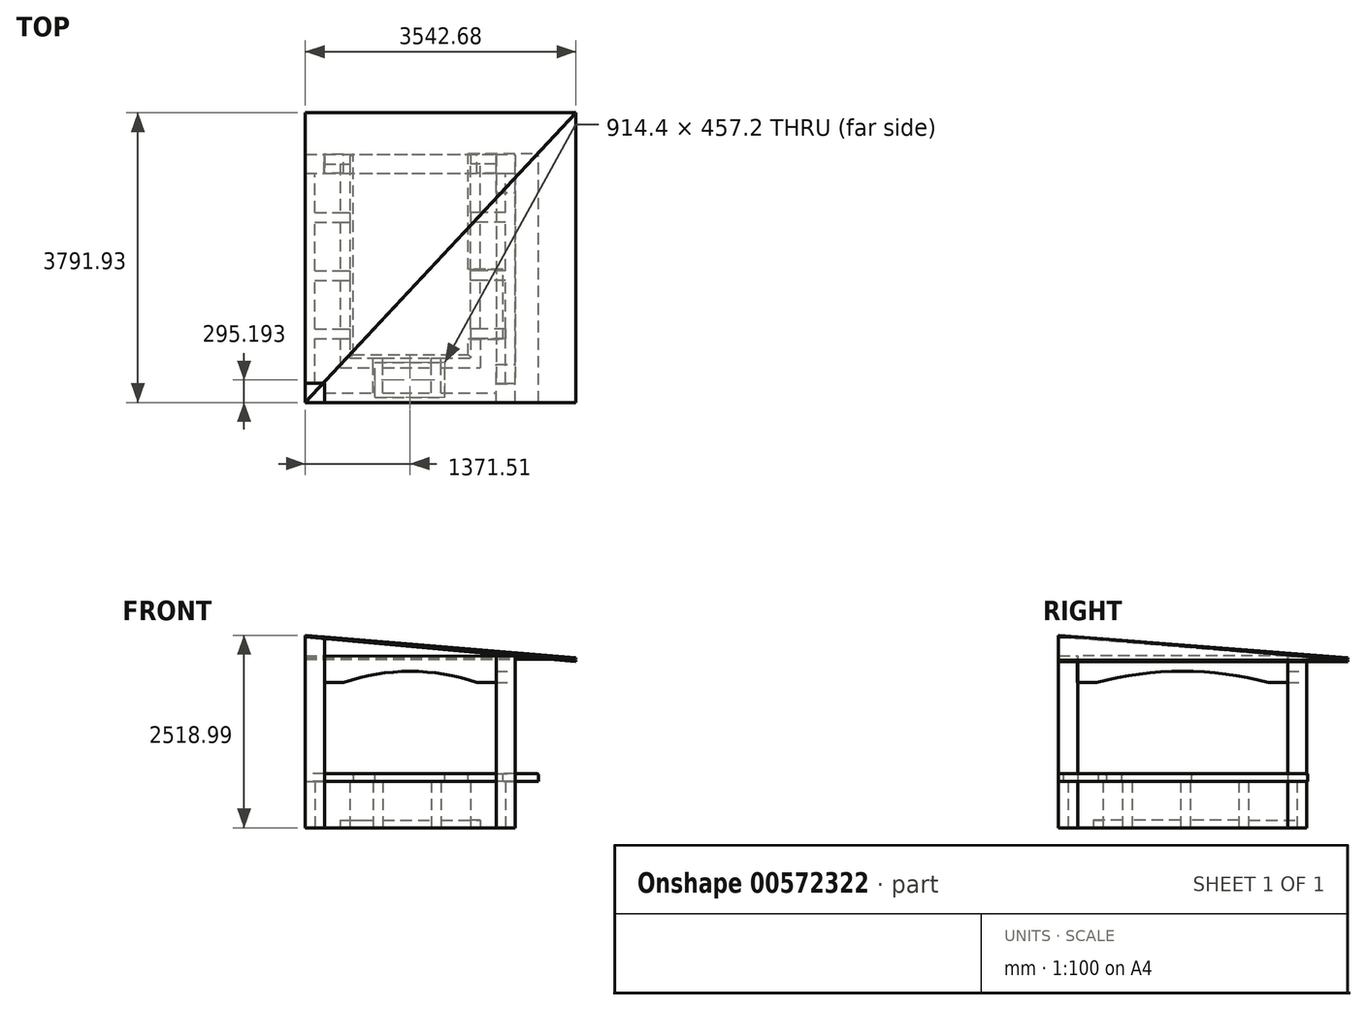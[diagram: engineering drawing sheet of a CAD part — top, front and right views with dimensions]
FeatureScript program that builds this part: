
annotation { "Feature Type Name" : "Feature", "Feature Type Description" : "" }
export const myFeature = defineFeature(function(context is Context, id is Id, definition is map)
    precondition{}
    {
        {
            var Q0;
            Q0=qCreatedBy(makeId("Top.planeOp"),FACE);
            var sketch = newSketch(context, id + "F0", { "sketchPlane" : qUnion([Q0])});
            skLineSegment(sketch, "E0.bottom", {"start": v(0, 0) * mm, "end": v(250, 0) * mm});
            skLineSegment(sketch, "E0.top", {"start": v(0, 250) * mm, "end": v(250, 250) * mm});
            skLineSegment(sketch, "E0.left", {"start": v(0, 0) * mm, "end": v(0, 250) * mm});
            skLineSegment(sketch, "E0.right", {"start": v(250, 0) * mm, "end": v(250, 250) * mm});
            skLineSegment(sketch, "E1.0.1.0", {"start": v(0, 3250) * mm, "end": v(250, 3250) * mm});
            skLineSegment(sketch, "E1.0.1.1", {"start": v(0, 3000) * mm, "end": v(0, 3250) * mm});
            skLineSegment(sketch, "E1.0.1.2", {"start": v(0, 3000) * mm, "end": v(250, 3000) * mm});
            skLineSegment(sketch, "E1.0.1.3", {"start": v(250, 3000) * mm, "end": v(250, 3250) * mm});
            skLineSegment(sketch, "E1.1.0.0", {"start": v(2500, 250) * mm, "end": v(2750, 250) * mm});
            skLineSegment(sketch, "E1.1.0.1", {"start": v(2500, 0) * mm, "end": v(2500, 250) * mm});
            skLineSegment(sketch, "E1.1.0.2", {"start": v(2500, 0) * mm, "end": v(2750, 0) * mm});
            skLineSegment(sketch, "E1.1.0.3", {"start": v(2750, 0) * mm, "end": v(2750, 250) * mm});
            skLineSegment(sketch, "E1.1.1.0", {"start": v(2500, 3250) * mm, "end": v(2750, 3250) * mm});
            skLineSegment(sketch, "E1.1.1.1", {"start": v(2500, 3000) * mm, "end": v(2500, 3250) * mm});
            skLineSegment(sketch, "E1.1.1.2", {"start": v(2500, 3000) * mm, "end": v(2750, 3000) * mm});
            skLineSegment(sketch, "E1.1.1.3", {"start": v(2750, 3000) * mm, "end": v(2750, 3250) * mm});
            skLineSegment(sketch, "E1.direction2", {"start": v(0, 250) * mm, "end": v(0, 3250) * mm, "construction": true});
            skLineSegment(sketch, "E2.bottom", {"start": v(0, 250) * mm, "end": v(127, 250) * mm});
            skLineSegment(sketch, "E2.top", {"start": v(0, 3250) * mm, "end": v(127, 3250) * mm});
            skLineSegment(sketch, "E2.left", {"start": v(0, 250) * mm, "end": v(0, 3250) * mm});
            skLineSegment(sketch, "E2.right", {"start": v(127, 250) * mm, "end": v(127, 3000) * mm});
            skLineSegment(sketch, "E3.bottom", {"start": v(250, 0) * mm, "end": v(2750, 0) * mm});
            skLineSegment(sketch, "E3.top", {"start": v(250, 127) * mm, "end": v(2500, 127) * mm});
            skLineSegment(sketch, "E3.left", {"start": v(250, 0) * mm, "end": v(250, 127) * mm});
            skLineSegment(sketch, "E3.right", {"start": v(2750, 0) * mm, "end": v(2750, 127) * mm});
            skLineSegment(sketch, "E4.top", {"start": v(2750, 3250) * mm, "end": v(2623, 3250) * mm});
            skLineSegment(sketch, "E4.left", {"start": v(2750, 127) * mm, "end": v(2750, 3250) * mm});
            skLineSegment(sketch, "E4.right", {"start": v(2623, 250) * mm, "end": v(2623, 3000) * mm});
            skLineSegment(sketch, "E5.bottom", {"start": v(2623, 3250) * mm, "end": v(2165.8, 3250) * mm});
            skLineSegment(sketch, "E5.top", {"start": v(2500, 3123) * mm, "end": v(2165.8, 3123) * mm});
            skLineSegment(sketch, "E5.right", {"start": v(2165.8, 3250) * mm, "end": v(2165.8, 3123) * mm});
            skLineSegment(sketch, "E6.bottom", {"start": v(127, 3250) * mm, "end": v(584.2, 3250) * mm});
            skLineSegment(sketch, "E6.top", {"start": v(250, 3123) * mm, "end": v(584.2, 3123) * mm});
            skLineSegment(sketch, "E6.right", {"start": v(584.2, 3250) * mm, "end": v(584.2, 3123) * mm});
            skLineSegment(sketch, "E7.0.1.0", {"start": v(127, 2488) * mm, "end": v(584.2, 2488) * mm});
            skLineSegment(sketch, "E7.0.1.1", {"start": v(127, 2361) * mm, "end": v(584.2, 2361) * mm});
            skLineSegment(sketch, "E7.0.1.2", {"start": v(584.2, 2488) * mm, "end": v(584.2, 2361) * mm});
            skLineSegment(sketch, "E7.0.1.3", {"start": v(127, 2488) * mm, "end": v(127, 2361) * mm});
            skLineSegment(sketch, "E7.0.2.0", {"start": v(127, 1726) * mm, "end": v(584.2, 1726) * mm});
            skLineSegment(sketch, "E7.0.2.1", {"start": v(127, 1599) * mm, "end": v(584.2, 1599) * mm});
            skLineSegment(sketch, "E7.0.2.2", {"start": v(584.2, 1726) * mm, "end": v(584.2, 1599) * mm});
            skLineSegment(sketch, "E7.0.2.3", {"start": v(127, 1726) * mm, "end": v(127, 1599) * mm});
            skLineSegment(sketch, "E7.direction2", {"start": v(127, 3000) * mm, "end": v(127, 2488) * mm, "construction": true});
            skLineSegment(sketch, "E8.0.1.0", {"start": v(2623, 2361) * mm, "end": v(2165.8, 2361) * mm});
            skLineSegment(sketch, "E8.0.1.1", {"start": v(2623, 2488) * mm, "end": v(2165.8, 2488) * mm});
            skLineSegment(sketch, "E8.0.1.2", {"start": v(2623, 2488) * mm, "end": v(2623, 2361) * mm});
            skLineSegment(sketch, "E8.0.1.3", {"start": v(2165.8, 2488) * mm, "end": v(2165.8, 2361) * mm});
            skLineSegment(sketch, "E8.0.2.0", {"start": v(2623.2, 836.8) * mm, "end": v(2166, 836.8) * mm});
            skLineSegment(sketch, "E8.0.2.1", {"start": v(2623.2, 964) * mm, "end": v(2166, 964) * mm});
            skLineSegment(sketch, "E8.0.2.2", {"start": v(2623.2, 964) * mm, "end": v(2623.2, 836.8) * mm});
            skLineSegment(sketch, "E8.0.2.3", {"start": v(2166, 964) * mm, "end": v(2166, 836.8) * mm});
            skLineSegment(sketch, "E8.direction2", {"start": v(2165.8, 3123) * mm, "end": v(2165.8, 2361) * mm, "construction": true});
            skLineSegment(sketch, "E9.bottom", {"start": v(889, 127) * mm, "end": v(1016, 127) * mm});
            skLineSegment(sketch, "E9.top", {"start": v(889, 584.2) * mm, "end": v(1016, 584.2) * mm});
            skLineSegment(sketch, "E9.left", {"start": v(889, 127) * mm, "end": v(889, 584.2) * mm});
            skLineSegment(sketch, "E9.right", {"start": v(1016, 127) * mm, "end": v(1016, 584.2) * mm});
            skLineSegment(sketch, "E10.1.0.0", {"start": v(1651, 127) * mm, "end": v(1651, 584.2) * mm});
            skLineSegment(sketch, "E10.1.0.1", {"start": v(1778, 127) * mm, "end": v(1778, 584.2) * mm});
            skLineSegment(sketch, "E10.1.0.2", {"start": v(1651, 127) * mm, "end": v(1778, 127) * mm});
            skLineSegment(sketch, "E10.1.0.3", {"start": v(1651, 584.2) * mm, "end": v(1778, 584.2) * mm});
            skLineSegment(sketch, "E11.bottom", {"start": v(584.2, 3123) * mm, "end": v(457.2, 3123) * mm});
            skLineSegment(sketch, "E11.top", {"start": v(584.2, 2488) * mm, "end": v(457.2, 2488) * mm});
            skLineSegment(sketch, "E11.left", {"start": v(584.2, 3123) * mm, "end": v(584.2, 2488) * mm});
            skLineSegment(sketch, "E11.right", {"start": v(457.2, 3123) * mm, "end": v(457.2, 2488) * mm});
            skLineSegment(sketch, "E12.bottom", {"start": v(584.2, 2361) * mm, "end": v(457.2, 2361) * mm});
            skLineSegment(sketch, "E12.top", {"start": v(584.2, 1726) * mm, "end": v(457.2, 1726) * mm});
            skLineSegment(sketch, "E12.left", {"start": v(584.2, 2361) * mm, "end": v(584.2, 1726) * mm});
            skLineSegment(sketch, "E12.right", {"start": v(457.2, 2361) * mm, "end": v(457.2, 1726) * mm});
            skLineSegment(sketch, "E13.bottom", {"start": v(584.2, 1599) * mm, "end": v(457.2, 1599) * mm});
            skLineSegment(sketch, "E13.top", {"start": v(584.2, 584.2) * mm, "end": v(457.2, 584.2) * mm});
            skLineSegment(sketch, "E13.left", {"start": v(584.2, 1599) * mm, "end": v(584.2, 584.2) * mm});
            skLineSegment(sketch, "E13.right", {"start": v(457.2, 1599) * mm, "end": v(457.2, 964) * mm});
            skLineSegment(sketch, "E14.bottom", {"start": v(457.2, 584.2) * mm, "end": v(889, 584.2) * mm});
            skLineSegment(sketch, "E14.top", {"start": v(457.2, 457.2) * mm, "end": v(889, 457.2) * mm});
            skLineSegment(sketch, "E14.left", {"start": v(457.2, 584.2) * mm, "end": v(457.2, 457.2) * mm});
            skLineSegment(sketch, "E14.right", {"start": v(889, 584.2) * mm, "end": v(889, 457.2) * mm});
            skLineSegment(sketch, "E15.bottom", {"start": v(1016, 584.2) * mm, "end": v(1651, 584.2) * mm});
            skLineSegment(sketch, "E15.top", {"start": v(1016, 457.2) * mm, "end": v(1651, 457.2) * mm});
            skLineSegment(sketch, "E15.left", {"start": v(1016, 584.2) * mm, "end": v(1016, 457.2) * mm});
            skLineSegment(sketch, "E15.right", {"start": v(1651, 584.2) * mm, "end": v(1651, 457.2) * mm});
            skLineSegment(sketch, "E16.bottom", {"start": v(1778, 584.2) * mm, "end": v(2293, 584.2) * mm});
            skLineSegment(sketch, "E16.left", {"start": v(1778, 584.2) * mm, "end": v(1778, 457.2) * mm});
            skLineSegment(sketch, "E17.bottom", {"start": v(2166, 836.8) * mm, "end": v(2293, 836.8) * mm});
            skLineSegment(sketch, "E17.top", {"start": v(1778, 457.2) * mm, "end": v(2293, 457.2) * mm});
            skLineSegment(sketch, "E17.right", {"start": v(2293, 836.8) * mm, "end": v(2293, 457.2) * mm});
            skLineSegment(sketch, "E18.bottom", {"start": v(2166, 964) * mm, "end": v(2293, 964) * mm});
            skLineSegment(sketch, "E18.top", {"start": v(2166, 2361) * mm, "end": v(2293, 2361) * mm});
            skLineSegment(sketch, "E18.left", {"start": v(2166, 964) * mm, "end": v(2166, 2361) * mm});
            skLineSegment(sketch, "E18.right", {"start": v(2293, 964) * mm, "end": v(2293, 1599) * mm});
            skLineSegment(sketch, "E19.bottom", {"start": v(2165.8, 2488) * mm, "end": v(2293, 2488) * mm});
            skLineSegment(sketch, "E19.top", {"start": v(2165.8, 3123) * mm, "end": v(2293, 3123) * mm});
            skLineSegment(sketch, "E19.left", {"start": v(2165.8, 2488) * mm, "end": v(2165.8, 3123) * mm});
            skLineSegment(sketch, "E19.right", {"start": v(2293, 2488) * mm, "end": v(2293, 3123) * mm});
            skLineSegment(sketch, "E20.0.0.3", {"start": v(127, 964) * mm, "end": v(584.2, 964) * mm});
            skLineSegment(sketch, "E20.3.0.3", {"start": v(127, 837) * mm, "end": v(584.2, 837) * mm});
            skLineSegment(sketch, "E20.6.0.3", {"start": v(584.2, 964) * mm, "end": v(584.2, 837) * mm});
            skLineSegment(sketch, "E20.9.0.3", {"start": v(127, 964) * mm, "end": v(127, 837) * mm});
            skLineSegment(sketch, "E21.bottom", {"start": v(2623, 1726) * mm, "end": v(2166, 1726) * mm});
            skLineSegment(sketch, "E21.top", {"start": v(2623, 1599) * mm, "end": v(2166, 1599) * mm});
            skLineSegment(sketch, "E21.left", {"start": v(2623, 1726) * mm, "end": v(2623, 1599) * mm});
            skLineSegment(sketch, "E21.right", {"start": v(2166, 1726) * mm, "end": v(2166, 1599) * mm});
            skLineSegment(sketch, "E22.trimOffspring", {"start": v(2293, 1726) * mm, "end": v(2293, 2361) * mm});
            skLineSegment(sketch, "E23.trimOffspring", {"start": v(457.2, 837) * mm, "end": v(457.2, 584.2) * mm});
            skLineSegment(sketch, "E24", {"start": v(2166, 836.8) * mm, "end": v(2166, 584.2) * mm});
            skSolve(sketch);
        }
        {
            var Q0;
            {var subQ4=sQuery(id+"F0.wireOp",EDGE,"E0.top");Q0=makeQuery(id+"F0.imprint","IMPRINT",FACE,{"disambiguationData":[TD([[makeQuery(id+"F0.imprint","IMPRINT",EDGE,{"derivedFrom":subQ4}),-1.0]])]});}
            extrude(context, id + "F1", {"entities" : qUnion([Q0]), "depth" : 2500 * mm, "offsetDistance" : 25.4 * mm});
        }
        {
            var Q0;
            {var subQ0=sQuery(id+"F0.wireOp",EDGE,"E1.0.1.0");Q0=makeQuery(id+"F0.imprint","IMPRINT",FACE,{"disambiguationData":[TD([[makeQuery(id+"F0.imprint","IMPRINT",EDGE,{"derivedFrom":subQ0}),-1.0]])]});}
            extrude(context, id + "F2", {"entities" : qUnion([Q0]), "depth" : 2250 * mm, "offsetDistance" : 25 * mm});
        }
        {
            var Q0;
            Q0=makeQuery(id+"F0.imprint","IMPRINT",FACE,{"disambiguationData":[TD([[makeQuery(id+"F0.imprint","IMPRINT",EDGE,{"derivedFrom":sQuery(id+"F0.wireOp",EDGE,"E1.1.0.0")}),-1.0]])]});
            extrude(context, id + "F3", {"entities" : qUnion([Q0]), "depth" : 2250 * mm, "offsetDistance" : 25 * mm});
        }
        {
            var Q0;
            Q0=makeQuery(id+"F0.imprint","IMPRINT",FACE,{"disambiguationData":[TD([[makeQuery(id+"F0.imprint","IMPRINT",EDGE,{"derivedFrom":sQuery(id+"F0.wireOp",EDGE,"E1.1.1.0")}),-1.0]])]});
            extrude(context, id + "F4", {"entities" : qUnion([Q0]), "depth" : 2250 * mm, "offsetDistance" : 25 * mm});
        }
        {
            var Q0;
            {var subQ5=sQuery(id+"F0.wireOp",EDGE,"E6.bottom");Q0=makeQuery(id+"F0.imprint","IMPRINT",FACE,{"disambiguationData":[TD([[makeQuery(id+"F0.imprint","IMPRINT",EDGE,{"derivedFrom":subQ5}),-1.0]])]});}
            var Q1;
            {var subQ0=sQuery(id+"F0.wireOp",EDGE,"E2.left");Q1=makeQuery(id+"F0.imprint","IMPRINT",FACE,{"disambiguationData":[TD([[makeQuery(id+"F0.imprint","IMPRINT",EDGE,{"derivedFrom":subQ0}),-1.0]])]});}
            var Q2;
            {var subQ0=sQuery(id+"F0.wireOp",EDGE,"E7.0.1.2");Q2=makeQuery(id+"F0.imprint","IMPRINT",FACE,{"disambiguationData":[TD([[makeQuery(id+"F0.imprint","IMPRINT",EDGE,{"derivedFrom":subQ0}),-1.0]])]});}
            var Q3;
            {var subQ4=sQuery(id+"F0.wireOp",EDGE,"E7.0.2.2");Q3=makeQuery(id+"F0.imprint","IMPRINT",FACE,{"disambiguationData":[TD([[makeQuery(id+"F0.imprint","IMPRINT",EDGE,{"derivedFrom":subQ4}),-1.0]])]});}
            var Q4;
            {var subQ0=sQuery(id+"F0.wireOp",EDGE,"E20.0.0.3");var subQ4=sQuery(id+"F0.wireOp",EDGE,"E2.right");var subQ5=makeQuery(id+"F0.imprint","INTERSECT",VERTEX,{"derivedFrom":[subQ4,subQ0]});Q4=makeQuery(id+"F0.imprint","IMPRINT",FACE,{"disambiguationData":[TD([[makeQuery(id+"F0.imprint","IMPRINT",EDGE,{"disambiguationData":[TD([[subQ5,1.0]])],"derivedFrom":subQ4}),-1.0]])]});}
            var Q5;
            {var subQ1=sQuery(id+"F0.wireOp",EDGE,"E9.top");Q5=makeQuery(id+"F0.imprint","IMPRINT",FACE,{"disambiguationData":[TD([[makeQuery(id+"F0.imprint","IMPRINT",EDGE,{"derivedFrom":subQ1}),-1.0]])]});}
            var Q6;
            {var subQ4=sQuery(id+"F0.wireOp",EDGE,"E10.1.0.3");Q6=makeQuery(id+"F0.imprint","IMPRINT",FACE,{"disambiguationData":[TD([[makeQuery(id+"F0.imprint","IMPRINT",EDGE,{"derivedFrom":subQ4}),-1.0]])]});}
            var Q7;
            {var subQ0=sQuery(id+"F0.wireOp",EDGE,"E3.bottom");Q7=makeQuery(id+"F0.imprint","IMPRINT",FACE,{"disambiguationData":[TD([[makeQuery(id+"F0.imprint","IMPRINT",EDGE,{"derivedFrom":subQ0}),1.0]])]});}
            var Q8;
            {var subQ13=sQuery(id+"F0.wireOp",EDGE,"E4.left");Q8=makeQuery(id+"F0.imprint","IMPRINT",FACE,{"disambiguationData":[TD([[makeQuery(id+"F0.imprint","IMPRINT",EDGE,{"derivedFrom":subQ13}),1.0]])]});}
            var Q9;
            {var subQ0=sQuery(id+"F0.wireOp",EDGE,"E8.0.2.3");Q9=makeQuery(id+"F0.imprint","IMPRINT",FACE,{"disambiguationData":[TD([[makeQuery(id+"F0.imprint","IMPRINT",EDGE,{"derivedFrom":subQ0}),1.0]])]});}
            var Q10;
            {var subQ0=sQuery(id+"F0.wireOp",EDGE,"E21.bottom");var subQ4=sQuery(id+"F0.wireOp",EDGE,"E4.right");var subQ5=makeQuery(id+"F0.imprint","INTERSECT",VERTEX,{"derivedFrom":[subQ4,subQ0]});Q10=makeQuery(id+"F0.imprint","IMPRINT",FACE,{"disambiguationData":[TD([[makeQuery(id+"F0.imprint","IMPRINT",EDGE,{"disambiguationData":[TD([[subQ5,1.0]])],"derivedFrom":subQ4}),1.0]])]});}
            var Q11;
            {var subQ0=sQuery(id+"F0.wireOp",EDGE,"E8.0.1.3");Q11=makeQuery(id+"F0.imprint","IMPRINT",FACE,{"disambiguationData":[TD([[makeQuery(id+"F0.imprint","IMPRINT",EDGE,{"derivedFrom":subQ0}),1.0]])]});}
            var Q12;
            {var subQ5=sQuery(id+"F0.wireOp",EDGE,"E5.bottom");Q12=makeQuery(id+"F0.imprint","IMPRINT",FACE,{"disambiguationData":[TD([[makeQuery(id+"F0.imprint","IMPRINT",EDGE,{"derivedFrom":subQ5}),1.0]])]});}
            extrude(context, id + "F5", {"entities" : qUnion([Q0, Q1, Q2, Q3, Q4, Q5, Q6, Q7, Q8, Q9, Q10, Q11, Q12]), "depth" : 609.6 * mm, "offsetDistance" : 25 * mm});
        }
        {
            var Q0;
            {var subQ0=sQuery(id+"F0.wireOp",EDGE,"E11.left");Q0=makeQuery(id+"F0.imprint","IMPRINT",FACE,{"disambiguationData":[TD([[makeQuery(id+"F0.imprint","IMPRINT",EDGE,{"derivedFrom":subQ0}),-1.0]])]});}
            var Q1;
            {var subQ0=sQuery(id+"F0.wireOp",EDGE,"E12.left");Q1=makeQuery(id+"F0.imprint","IMPRINT",FACE,{"disambiguationData":[TD([[makeQuery(id+"F0.imprint","IMPRINT",EDGE,{"derivedFrom":subQ0}),-1.0]])]});}
            var Q2;
            {var subQ3=sQuery(id+"F0.wireOp",EDGE,"E13.right");Q2=makeQuery(id+"F0.imprint","IMPRINT",FACE,{"disambiguationData":[TD([[makeQuery(id+"F0.imprint","IMPRINT",EDGE,{"derivedFrom":subQ3}),1.0]])]});}
            var Q3;
            {var subQ0=sQuery(id+"F0.wireOp",EDGE,"E13.top");Q3=makeQuery(id+"F0.imprint","IMPRINT",FACE,{"disambiguationData":[TD([[makeQuery(id+"F0.imprint","IMPRINT",EDGE,{"derivedFrom":subQ0}),-1.0]])]});}
            var Q4;
            Q4=makeQuery(id+"F0.imprint","IMPRINT",FACE,{"disambiguationData":[TD([[makeQuery(id+"F0.imprint","IMPRINT",EDGE,{"derivedFrom":sQuery(id+"F0.wireOp",EDGE,"E13.top")}),1.0]])]});
            var Q5;
            {var subQ0=sQuery(id+"F0.wireOp",EDGE,"E15.bottom");Q5=makeQuery(id+"F0.imprint","IMPRINT",FACE,{"disambiguationData":[TD([[makeQuery(id+"F0.imprint","IMPRINT",EDGE,{"derivedFrom":subQ0}),-1.0]])]});}
            var Q6;
            {var subQ0=sQuery(id+"F0.wireOp",EDGE,"E17.top");Q6=makeQuery(id+"F0.imprint","IMPRINT",FACE,{"disambiguationData":[TD([[makeQuery(id+"F0.imprint","IMPRINT",EDGE,{"derivedFrom":subQ0}),1.0]])]});}
            var Q7;
            {var subQ0=sQuery(id+"F0.wireOp",EDGE,"E24");Q7=makeQuery(id+"F0.imprint","IMPRINT",FACE,{"disambiguationData":[TD([[makeQuery(id+"F0.imprint","IMPRINT",EDGE,{"derivedFrom":subQ0}),1.0]])]});}
            var Q8;
            {var subQ3=sQuery(id+"F0.wireOp",EDGE,"E18.right");Q8=makeQuery(id+"F0.imprint","IMPRINT",FACE,{"disambiguationData":[TD([[makeQuery(id+"F0.imprint","IMPRINT",EDGE,{"derivedFrom":subQ3}),1.0]])]});}
            var Q9;
            {var subQ0=sQuery(id+"F0.wireOp",EDGE,"E22.trimOffspring");Q9=makeQuery(id+"F0.imprint","IMPRINT",FACE,{"disambiguationData":[TD([[makeQuery(id+"F0.imprint","IMPRINT",EDGE,{"derivedFrom":subQ0}),1.0]])]});}
            var Q10;
            {var subQ0=sQuery(id+"F0.wireOp",EDGE,"E19.left");Q10=makeQuery(id+"F0.imprint","IMPRINT",FACE,{"disambiguationData":[TD([[makeQuery(id+"F0.imprint","IMPRINT",EDGE,{"derivedFrom":subQ0}),-1.0]])]});}
            extrude(context, id + "F6", {"entities" : qUnion([Q0, Q1, Q2, Q3, Q4, Q5, Q6, Q7, Q8, Q9, Q10]), "depth" : 101.6 * mm, "offsetDistance" : 25 * mm});
        }
        {
            var Q0;
            Q0=makeQuery(id+"F5.opExtrude","CAP_FACE",FACE,{"disambiguationData":[OSD([sQuery(id+"F0.wireOp",EDGE,"E0.top"),sQuery(id+"F0.wireOp",EDGE,"E1.0.1.2"),sQuery(id+"F0.wireOp",EDGE,"E2.left"),sQuery(id+"F0.wireOp",EDGE,"E2.right"),sQuery(id+"F0.wireOp",EDGE,"E7.0.1.0"),sQuery(id+"F0.wireOp",EDGE,"E7.0.1.1"),sQuery(id+"F0.wireOp",EDGE,"E7.0.1.2"),sQuery(id+"F0.wireOp",EDGE,"E7.0.2.0"),sQuery(id+"F0.wireOp",EDGE,"E7.0.2.1"),sQuery(id+"F0.wireOp",EDGE,"E7.0.2.2"),sQuery(id+"F0.wireOp",EDGE,"E13.left"),sQuery(id+"F0.wireOp",EDGE,"E20.0.0.3"),sQuery(id+"F0.wireOp",EDGE,"E20.3.0.3")])],"isStart":false});
            var sketch = newSketch(context, id + "F7", { "sketchPlane" : qUnion([Q0])});
            skLineSegment(sketch, "E25.bottom", {"start": v(0, 0) * mm, "end": v(625, 0) * mm});
            skLineSegment(sketch, "E25.top", {"start": v(0, 3250) * mm, "end": v(625, 3250) * mm});
            skLineSegment(sketch, "E25.left", {"start": v(0, 0) * mm, "end": v(0, 3250) * mm});
            skLineSegment(sketch, "E25.right", {"start": v(625, 0) * mm, "end": v(625, 3250) * mm});
            skLineSegment(sketch, "E26.bottom", {"start": v(625, 0) * mm, "end": v(2133.48, 0) * mm});
            skLineSegment(sketch, "E26.top", {"start": v(625, 625.4) * mm, "end": v(2133.48, 625.4) * mm});
            skLineSegment(sketch, "E26.left", {"start": v(625, 0) * mm, "end": v(625, 625.4) * mm});
            skLineSegment(sketch, "E26.right", {"start": v(2133.48, 0) * mm, "end": v(2133.48, 625.4) * mm});
            skLineSegment(sketch, "E27.bottom", {"start": v(2133.48, 0) * mm, "end": v(3054.8, 0) * mm});
            skLineSegment(sketch, "E27.top", {"start": v(2133.48, 3263.7) * mm, "end": v(3054.8, 3263.7) * mm});
            skLineSegment(sketch, "E27.left", {"start": v(2133.48, 0) * mm, "end": v(2133.48, 3263.7) * mm});
            skLineSegment(sketch, "E27.right", {"start": v(3054.8, 0) * mm, "end": v(3054.8, 3263.7) * mm});
            skSolve(sketch);
        }
        {
            var Q0;
            Q0 = qSketchRegion(id + "F7", true);
            extrude(context, id + "F8", {"entities" : qUnion([Q0]), "depth" : 101.6 * mm, "offsetDistance" : 25 * mm});
        }
        {
            var Q0;
            Q0=makeQuery(id+"F8.opExtrude","CAP_EDGE",EDGE,{"disambiguationData":[OSD([sQuery(id+"F7.wireOp",EDGE,"E27.right")])],"isStart":false});
            var Q1;
            Q1=makeQuery(id+"F8.opExtrude","CAP_EDGE",EDGE,{"disambiguationData":[OSD([sQuery(id+"F7.wireOp",EDGE,"E27.top")])],"isStart":false});
            var Q2;
            Q2=makeQuery(id+"F8.opExtrude","CAP_EDGE",EDGE,{"disambiguationData":[OSD([sQuery(id+"F7.wireOp",EDGE,"E25.right")])],"isStart":false});
            var Q3;
            Q3=makeQuery(id+"F8.opExtrude","CAP_EDGE",EDGE,{"disambiguationData":[OSD([sQuery(id+"F7.wireOp",EDGE,"E25.top")])],"isStart":false});
            var Q4;
            Q4=makeQuery(id+"F8.opExtrude","CAP_EDGE",EDGE,{"disambiguationData":[OSD([sQuery(id+"F7.wireOp",EDGE,"E26.top")])],"isStart":false});
            var Q5;
            Q5=makeQuery(id+"F8.opExtrude","CAP_EDGE",EDGE,{"disambiguationData":[OSD([sQuery(id+"F7.wireOp",EDGE,"E27.left")])],"isStart":false});
            fillet(context, id + "F9", {"entities" : qUnion([Q0, Q1, Q2, Q3, Q4, Q5]), "tangentPropagation" : true, "radius" : 25.4 * mm, "defaultsChanged" : true, "vertexSettings" : [], "allowEdgeOverflow" : false});
        }
        {
            var Q0;
            Q0=makeQuery(id+"F2.opExtrude","CAP_VERTEX",VERTEX,{"disambiguationData":[OSD([sQuery(id+"F0.wireOp",EDGE,"E1.0.1.0"),sQuery(id+"F0.wireOp",EDGE,"E1.0.1.1")])],"isStart":false});
            var Q1;
            Q1=makeQuery(id+"F4.opExtrude","CAP_VERTEX",VERTEX,{"disambiguationData":[OSD([sQuery(id+"F0.wireOp",EDGE,"E1.1.1.0"),sQuery(id+"F0.wireOp",EDGE,"E1.1.1.3")])],"isStart":false});
            var Q2;
            Q2=makeQuery(id+"F1.opExtrude","CAP_VERTEX",VERTEX,{"disambiguationData":[OSD([sQuery(id+"F0.wireOp",EDGE,"E0.bottom"),sQuery(id+"F0.wireOp",EDGE,"E0.left")])],"isStart":false});
            cPlane(context, id + "F10", {"entities" : qUnion([Q0, Q1, Q2]), "cplaneType" : CPlaneType.THREE_POINT, "offset" : 25 * mm, "width" : 150 * mm, "height" : 150 * mm});
        }
        {
            var Q0;
            Q0=makeQuery(id+"F4.opExtrude","CAP_VERTEX",VERTEX,{"disambiguationData":[OSD([sQuery(id+"F0.wireOp",EDGE,"E1.1.1.0"),sQuery(id+"F0.wireOp",EDGE,"E1.1.1.3")])],"isStart":false});
            var Q1;
            Q1=makeQuery(id+"F3.opExtrude","CAP_VERTEX",VERTEX,{"disambiguationData":[OSD([sQuery(id+"F0.wireOp",EDGE,"E1.1.0.2"),sQuery(id+"F0.wireOp",EDGE,"E1.1.0.3")])],"isStart":false});
            var Q2;
            Q2=makeQuery(id+"F1.opExtrude","CAP_VERTEX",VERTEX,{"disambiguationData":[OSD([sQuery(id+"F0.wireOp",EDGE,"E0.bottom"),sQuery(id+"F0.wireOp",EDGE,"E0.left")])],"isStart":false});
            cPlane(context, id + "F11", {"entities" : qUnion([Q0, Q1, Q2]), "cplaneType" : CPlaneType.THREE_POINT, "offset" : 25 * mm, "width" : 150 * mm, "height" : 150 * mm});
        }
        {
            var Q0;
            Q0=makeQuery(id+"F4.opExtrude","SWEPT_FACE",FACE,{"disambiguationData":[OSD([sQuery(id+"F0.wireOp",EDGE,"E1.1.1.3")])]});
            var sketch = newSketch(context, id + "F12", { "sketchPlane" : qUnion([Q0])});
            skLineSegment(sketch, "E28", {"start": v(247.26, 1900) * mm, "end": v(497.26, 1900) * mm});
            skArc(sketch, "E29", {"start": v(2750, 1900) * mm, "mid": v(1623.63, 2050) * mm, "end": v(497.26, 1900) * mm});
            skLineSegment(sketch, "E30", {"start": v(2750, 1900) * mm, "end": v(3000, 1900) * mm});
            skLineSegment(sketch, "E31", {"start": v(3000, 1900) * mm, "end": v(3000, 2250) * mm});
            skLineSegment(sketch, "E32", {"start": v(3000, 2250) * mm, "end": v(247.26, 2250) * mm});
            skLineSegment(sketch, "E33", {"start": v(247.26, 2250) * mm, "end": v(247.26, 1900) * mm});
            skSolve(sketch);
        }
        {
            var Q0;
            Q0 = qSketchRegion(id + "F12", true);
            extrude(context, id + "F13", {"entities" : qUnion([Q0]), "oppositeDirection" : true, "depth" : 250 * mm, "offsetDistance" : 25 * mm});
        }
        {
            var Q0;
            Q0=makeQuery(id+"F4.opExtrude","SWEPT_FACE",FACE,{"disambiguationData":[OSD([sQuery(id+"F0.wireOp",EDGE,"E1.1.1.0")])]});
            var sketch = newSketch(context, id + "F14", { "sketchPlane" : qUnion([Q0])});
            skLineSegment(sketch, "E34", {"start": v(-2500, 2250) * mm, "end": v(-2500, 1900) * mm});
            skLineSegment(sketch, "E35", {"start": v(-2500, 1900) * mm, "end": v(-2250, 1900) * mm});
            skArc(sketch, "E36", {"start": v(-498.96, 1900) * mm, "mid": v(-1374.48, 2047.9) * mm, "end": v(-2250, 1900) * mm});
            skLineSegment(sketch, "E37", {"start": v(-498.96, 1900) * mm, "end": v(-248.96, 1900) * mm});
            skLineSegment(sketch, "E38", {"start": v(-248.96, 1900) * mm, "end": v(-248.96, 2245.82) * mm});
            skLineSegment(sketch, "E39", {"start": v(-248.96, 2245.82) * mm, "end": v(-2500, 2250) * mm});
            skSolve(sketch);
        }
        {
            var Q0;
            Q0=makeQuery(id+"F14.imprint","IMPRINT",FACE,{"disambiguationData":[TD([[makeQuery(id+"F14.imprint","IMPRINT",EDGE,{"derivedFrom":sQuery(id+"F14.wireOp",EDGE,"E35")}),1.0]])]});
            extrude(context, id + "F15", {"entities" : qUnion([Q0]), "oppositeDirection" : true, "depth" : 250 * mm, "offsetDistance" : 25 * mm});
        }
        {
            var Q0;
            Q0=qCreatedBy(id+"F10.planeOp",FACE);
            var sketch = newSketch(context, id + "F16", { "sketchPlane" : qUnion([Q0])});
            skLineSegment(sketch, "E40", {"start": v(0, -191.65) * mm, "end": v(0, 3609.92) * mm});
            skLineSegment(sketch, "E41", {"start": v(0, 3609.92) * mm, "end": v(3541.16, 3609.92) * mm});
            skLineSegment(sketch, "E42", {"start": v(3541.16, 3609.92) * mm, "end": v(0, -191.65) * mm});
            skSolve(sketch);
        }
        {
            var Q0;
            Q0 = qSketchRegion(id + "F16", true);
            extrude(context, id + "F17", {"entities" : qUnion([Q0]), "depth" : 19.05 * mm, "offsetDistance" : 25 * mm});
        }
        {
            var Q0;
            Q0=qCreatedBy(id+"F11.planeOp",FACE);
            var sketch = newSketch(context, id + "F18", { "sketchPlane" : qUnion([Q0])});
            skLineSegment(sketch, "E43", {"start": v(-226.37, 0) * mm, "end": v(3329.2, 0) * mm});
            skLineSegment(sketch, "E44", {"start": v(3329.2, 0) * mm, "end": v(3329.2, 3791.71) * mm});
            skLineSegment(sketch, "E45", {"start": v(3329.2, 3791.71) * mm, "end": v(-226.37, 0) * mm});
            skSolve(sketch);
        }
        {
            var Q0;
            Q0 = qSketchRegion(id + "F18", true);
            extrude(context, id + "F19", {"entities" : qUnion([Q0]), "depth" : 19.05 * mm, "offsetDistance" : 25 * mm});
        }
        {
            var Q0;
            Q0=makeQuery(id+"F8.opExtrude","CAP_FACE",FACE,{"disambiguationData":[OSD([sQuery(id+"F7.wireOp",EDGE,"E25.bottom"),sQuery(id+"F7.wireOp",EDGE,"E25.top"),sQuery(id+"F7.wireOp",EDGE,"E25.left"),sQuery(id+"F7.wireOp",EDGE,"E25.right"),sQuery(id+"F7.wireOp",EDGE,"E26.bottom"),sQuery(id+"F7.wireOp",EDGE,"E26.top"),sQuery(id+"F7.wireOp",EDGE,"E27.bottom"),sQuery(id+"F7.wireOp",EDGE,"E27.top"),sQuery(id+"F7.wireOp",EDGE,"E27.left"),sQuery(id+"F7.wireOp",EDGE,"E27.right")])],"isStart":false});
            var sketch = newSketch(context, id + "F20", { "sketchPlane" : qUnion([Q0])});
            skLineSegment(sketch, "E46.bottom", {"start": v(2133.48, 828.6) * mm, "end": v(2590.68, 828.6) * mm});
            skLineSegment(sketch, "E46.top", {"start": v(2133.48, 1743) * mm, "end": v(2590.68, 1743) * mm});
            skLineSegment(sketch, "E46.left", {"start": v(2133.48, 828.6) * mm, "end": v(2133.48, 1743) * mm});
            skLineSegment(sketch, "E46.right", {"start": v(2590.68, 828.6) * mm, "end": v(2590.68, 1743) * mm});
            skSolve(sketch);
        }
        {
            var Q0;
            Q0 = qSketchRegion(id + "F20", true);
            extrude(context, id + "F21", {"entities" : qUnion([Q0]), "operationType" : NewBodyOperationType.REMOVE, "endBound" : BoundingType.UP_TO_NEXT, "oppositeDirection" : true, "depth" : 25 * mm, "offsetDistance" : 25 * mm});
        }
        {
            var Q0;
            Q0=makeQuery(id+"F8.opExtrude","CAP_FACE",FACE,{"disambiguationData":[OSD([sQuery(id+"F7.wireOp",EDGE,"E25.bottom"),sQuery(id+"F7.wireOp",EDGE,"E25.top"),sQuery(id+"F7.wireOp",EDGE,"E25.left"),sQuery(id+"F7.wireOp",EDGE,"E25.right"),sQuery(id+"F7.wireOp",EDGE,"E26.bottom"),sQuery(id+"F7.wireOp",EDGE,"E26.top"),sQuery(id+"F7.wireOp",EDGE,"E27.bottom"),sQuery(id+"F7.wireOp",EDGE,"E27.top"),sQuery(id+"F7.wireOp",EDGE,"E27.left"),sQuery(id+"F7.wireOp",EDGE,"E27.right")])],"isStart":false});
            var sketch = newSketch(context, id + "F22", { "sketchPlane" : qUnion([Q0])});
            skLineSegment(sketch, "E47.bottom", {"start": v(914.28, 66.6) * mm, "end": v(1828.68, 66.6) * mm});
            skLineSegment(sketch, "E47.top", {"start": v(914.28, 523.8) * mm, "end": v(1828.68, 523.8) * mm});
            skLineSegment(sketch, "E47.left", {"start": v(914.28, 66.6) * mm, "end": v(914.28, 523.8) * mm});
            skLineSegment(sketch, "E47.right", {"start": v(1828.68, 66.6) * mm, "end": v(1828.68, 523.8) * mm});
            skSolve(sketch);
        }
        {
            var Q0;
            Q0 = qSketchRegion(id + "F22", true);
            extrude(context, id + "F23", {"entities" : qUnion([Q0]), "operationType" : NewBodyOperationType.REMOVE, "endBound" : BoundingType.UP_TO_NEXT, "oppositeDirection" : true, "depth" : 25 * mm, "offsetDistance" : 25 * mm});
        }
        {
            var Q0;
            Q0=makeQuery(id+"F2.opExtrude","SWEPT_BODY",BODY,{"disambiguationData":[OSD([sQuery(id+"F0.wireOp",EDGE,"E1.0.1.0"),sQuery(id+"F0.wireOp",EDGE,"E1.0.1.1"),sQuery(id+"F0.wireOp",EDGE,"E1.0.1.2"),sQuery(id+"F0.wireOp",EDGE,"E1.0.1.3")])]});
            var Q1;
            Q1=makeQuery(id+"F4.opExtrude","SWEPT_BODY",BODY,{"disambiguationData":[OSD([sQuery(id+"F0.wireOp",EDGE,"E1.1.1.0"),sQuery(id+"F0.wireOp",EDGE,"E1.1.1.1"),sQuery(id+"F0.wireOp",EDGE,"E1.1.1.2"),sQuery(id+"F0.wireOp",EDGE,"E1.1.1.3")])]});
            var Q2;
            Q2=makeQuery(id+"F3.opExtrude","SWEPT_BODY",BODY,{"disambiguationData":[OSD([sQuery(id+"F0.wireOp",EDGE,"E1.1.0.0"),sQuery(id+"F0.wireOp",EDGE,"E1.1.0.1"),sQuery(id+"F0.wireOp",EDGE,"E1.1.0.2"),sQuery(id+"F0.wireOp",EDGE,"E1.1.0.3")])]});
            var Q3;
            Q3=makeQuery(id+"F1.opExtrude","SWEPT_BODY",BODY,{"disambiguationData":[OSD([sQuery(id+"F0.wireOp",EDGE,"E0.bottom"),sQuery(id+"F0.wireOp",EDGE,"E0.top"),sQuery(id+"F0.wireOp",EDGE,"E0.left"),sQuery(id+"F0.wireOp",EDGE,"E0.right")])]});
            var Q4;
            Q4=makeQuery(id+"F8.opExtrude","SWEPT_BODY",BODY,{"disambiguationData":[OSD([sQuery(id+"F7.wireOp",EDGE,"E25.bottom"),sQuery(id+"F7.wireOp",EDGE,"E25.top"),sQuery(id+"F7.wireOp",EDGE,"E25.left"),sQuery(id+"F7.wireOp",EDGE,"E25.right"),sQuery(id+"F7.wireOp",EDGE,"E26.bottom"),sQuery(id+"F7.wireOp",EDGE,"E26.top"),sQuery(id+"F7.wireOp",EDGE,"E27.bottom"),sQuery(id+"F7.wireOp",EDGE,"E27.top"),sQuery(id+"F7.wireOp",EDGE,"E27.left"),sQuery(id+"F7.wireOp",EDGE,"E27.right")])]});
            booleanBodies(context, id + "F24", {"operationType" : BooleanOperationType.SUBTRACTION, "tools" : qUnion([Q0, Q1, Q2, Q3]), "targets" : qUnion([Q4]), "keepTools" : true});
        }
    });
